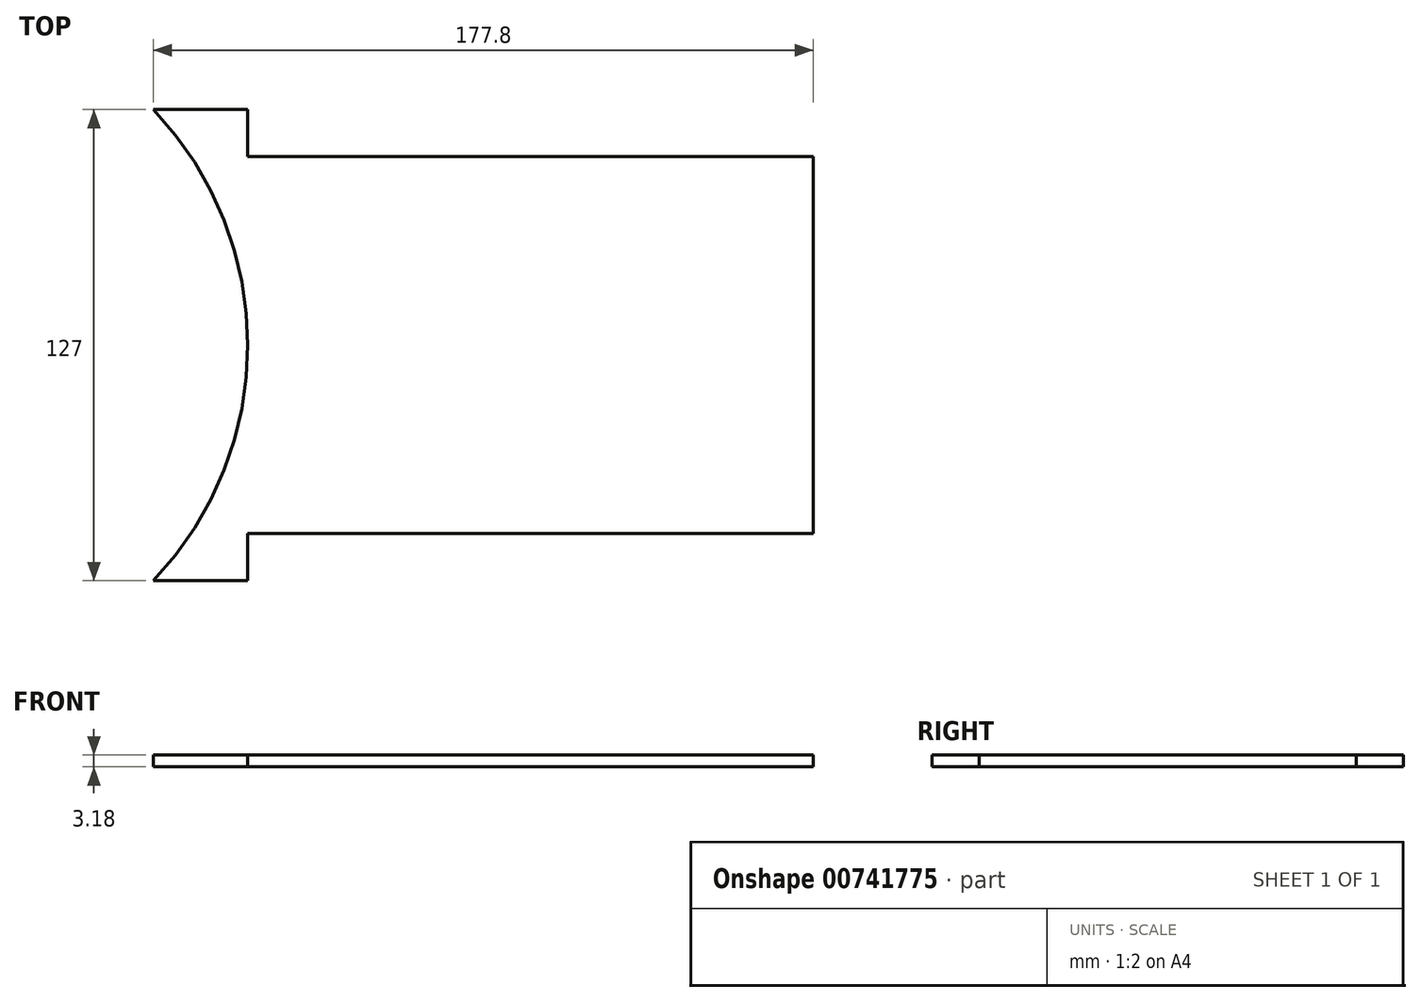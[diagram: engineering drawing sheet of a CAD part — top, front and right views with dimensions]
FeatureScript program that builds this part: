
annotation { "Feature Type Name" : "Feature", "Feature Type Description" : "" }
export const myFeature = defineFeature(function(context is Context, id is Id, definition is map)
    precondition{}
    {
        {
            var Q0;
            Q0=qCreatedBy(makeId("Top.planeOp"),FACE);
            var sketch = newSketch(context, id + "F0", { "sketchPlane" : qUnion([Q0])});
            skLineSegment(sketch, "E0.bottom", {"start": v(-120.07, 14.71) * mm, "end": v(57.73, 14.71) * mm});
            skLineSegment(sketch, "E0.top", {"start": v(-120.07, -86.89) * mm, "end": v(57.73, -86.89) * mm});
            skLineSegment(sketch, "E0.left", {"start": v(-120.07, 14.71) * mm, "end": v(-120.07, -86.89) * mm});
            skLineSegment(sketch, "E0.right", {"start": v(57.73, 14.71) * mm, "end": v(57.73, -86.89) * mm});
            skLineSegment(sketch, "E1.bottom", {"start": v(19.63, 14.71) * mm, "end": v(45.03, 14.71) * mm});
            skLineSegment(sketch, "E1.top", {"start": v(19.63, 11.54) * mm, "end": v(45.03, 11.54) * mm});
            skLineSegment(sketch, "E1.left", {"start": v(19.63, 14.71) * mm, "end": v(19.63, 11.54) * mm});
            skLineSegment(sketch, "E1.right", {"start": v(45.03, 14.71) * mm, "end": v(45.03, 11.54) * mm});
            skLineSegment(sketch, "E2.bottom", {"start": v(19.63, -83.71) * mm, "end": v(45.03, -83.71) * mm});
            skLineSegment(sketch, "E2.top", {"start": v(19.63, -86.89) * mm, "end": v(45.03, -86.89) * mm});
            skLineSegment(sketch, "E2.left", {"start": v(19.63, -83.71) * mm, "end": v(19.63, -86.89) * mm});
            skLineSegment(sketch, "E2.right", {"start": v(45.03, -83.71) * mm, "end": v(45.03, -86.89) * mm});
            skLineSegment(sketch, "E3.bottom", {"start": v(-120.07, 14.71) * mm, "end": v(-120.07, 14.71) * mm});
            skLineSegment(sketch, "E3.top", {"start": v(-120.07, 27.41) * mm, "end": v(-120.07, 27.41) * mm});
            skLineSegment(sketch, "E3.left", {"start": v(-120.07, 14.71) * mm, "end": v(-120.07, 27.41) * mm});
            skLineSegment(sketch, "E3.right", {"start": v(-120.07, 14.71) * mm, "end": v(-120.07, 27.41) * mm});
            skLineSegment(sketch, "E4.top", {"start": v(-89.1, 14.71) * mm, "end": v(-94.67, 14.71) * mm});
            skLineSegment(sketch, "E4.right", {"start": v(-94.67, 27.41) * mm, "end": v(-94.67, 14.71) * mm});
            skLineSegment(sketch, "E5.bottom", {"start": v(-120.07, 27.41) * mm, "end": v(-94.67, 27.41) * mm});
            skPoint(sketch, "E4.left.start.orphan", {"position": v(-89.1, 27.41) * mm});
            skLineSegment(sketch, "E6.bottom", {"start": v(-120.07, -86.89) * mm, "end": v(-120.07, -86.89) * mm});
            skLineSegment(sketch, "E6.top", {"start": v(-120.07, -99.59) * mm, "end": v(-120.07, -99.59) * mm});
            skLineSegment(sketch, "E6.left", {"start": v(-120.07, -86.89) * mm, "end": v(-120.07, -99.59) * mm});
            skLineSegment(sketch, "E6.right", {"start": v(-120.07, -86.89) * mm, "end": v(-120.07, -99.59) * mm});
            skLineSegment(sketch, "E7.bottom", {"start": v(-94.67, -99.59) * mm, "end": v(-94.67, -99.59) * mm});
            skLineSegment(sketch, "E7.top", {"start": v(-94.67, -86.89) * mm, "end": v(-94.67, -86.89) * mm});
            skLineSegment(sketch, "E7.left", {"start": v(-94.67, -99.59) * mm, "end": v(-94.67, -86.89) * mm});
            skLineSegment(sketch, "E7.right", {"start": v(-94.67, -99.59) * mm, "end": v(-94.67, -86.89) * mm});
            skLineSegment(sketch, "E8.bottom", {"start": v(-94.67, -99.59) * mm, "end": v(-120.07, -99.59) * mm});
            skLineSegment(sketch, "E8.top", {"start": v(-94.67, -99.59) * mm, "end": v(-120.07, -99.59) * mm});
            skArc(sketch, "E9", {"start": v(-120.07, -99.59) * mm, "mid": v(-94.67, -36.09) * mm, "end": v(-120.07, 27.41) * mm});
            skSolve(sketch);
        }
        {
            var Q0;
            {var subQ0=sQuery(id+"F0.wireOp",EDGE,"E4.right");var subQ7=sQuery(id+"F0.wireOp",EDGE,"E3.left");var subQ11=sQuery(id+"F0.wireOp",EDGE,"E6.left");var subQ12=sQuery(id+"F0.wireOp",EDGE,"E0.left");var subQ21=makeQuery(id+"F0.imprint","IMPRINT",EDGE,{"derivedFrom":sQuery(id+"F0.wireOp",EDGE,"E2.bottom")});var subQ23=sQuery(id+"F0.wireOp",EDGE,"E0.right");var subQ24=sQuery(id+"F0.wireOp",EDGE,"E7.left");var subQ30=makeQuery(id+"F0.imprint","IMPRINT",EDGE,{"derivedFrom":sQuery(id+"F0.wireOp",EDGE,"E1.top")});Q0=qUnion([makeQuery(id+"F0.imprint","IMPRINT",FACE,{"disambiguationData":[TD([[makeQuery(id+"F0.imprint","IMPRINT",EDGE,{"derivedFrom":subQ7}),-1.0]])]}),makeQuery(id+"F0.imprint","IMPRINT",FACE,{"disambiguationData":[TD([[makeQuery(id+"F0.imprint","IMPRINT",EDGE,{"derivedFrom":subQ12}),1.0]])]}),makeQuery(id+"F0.imprint","IMPRINT",FACE,{"disambiguationData":[TD([[subQ30,1.0]])]}),makeQuery(id+"F0.imprint","IMPRINT",FACE,{"disambiguationData":[TD([[makeQuery(id+"F0.imprint","IMPRINT",EDGE,{"derivedFrom":subQ24}),1.0]])]}),makeQuery(id+"F0.imprint","IMPRINT",FACE,{"disambiguationData":[TD([[makeQuery(id+"F0.imprint","IMPRINT",EDGE,{"derivedFrom":subQ23}),-1.0]])]}),makeQuery(id+"F0.imprint","IMPRINT",FACE,{"disambiguationData":[TD([[subQ21,-1.0]])]}),makeQuery(id+"F0.imprint","IMPRINT",FACE,{"disambiguationData":[TD([[makeQuery(id+"F0.imprint","IMPRINT",EDGE,{"derivedFrom":subQ11}),1.0]])]}),makeQuery(id+"F0.imprint","IMPRINT",FACE,{"disambiguationData":[TD([[makeQuery(id+"F0.imprint","IMPRINT",EDGE,{"derivedFrom":subQ0}),-1.0]])]})]);}
            extrude(context, id + "F1", {"entities" : qUnion([Q0]), "depth" : 3.17 * mm, "offsetDistance" : 25.4 * mm});
        }
        {
            var Q0;
            Q0=sQuery(id+"F0.wireOp",EDGE,"E1.top");
            var Q1;
            Q1=sQuery(id+"F0.wireOp",EDGE,"E1.left");
            var Q2;
            Q2=sQuery(id+"F0.wireOp",EDGE,"E1.right");
            extrude(context, id + "F2", {"bodyType" : ToolBodyType.SURFACE, "surfaceEntities" : qUnion([Q0, Q1, Q2]), "depth" : 25.4 * mm, "offsetDistance" : 25.4 * mm});
        }
        {
            var Q0;
            Q0=sQuery(id+"F0.wireOp",EDGE,"E2.bottom");
            var Q1;
            Q1=sQuery(id+"F0.wireOp",EDGE,"E2.top");
            var Q2;
            Q2=sQuery(id+"F0.wireOp",EDGE,"E2.right");
            var Q3;
            Q3=sQuery(id+"F0.wireOp",EDGE,"E2.left");
            extrude(context, id + "F3", {"bodyType" : ToolBodyType.SURFACE, "surfaceEntities" : qUnion([Q0, Q1, Q2, Q3]), "depth" : 25.4 * mm, "offsetDistance" : 25.4 * mm});
        }
        {
            var Q0;
            Q0=makeQuery(id+"F3.opExtrude","SWEPT_FACE",FACE,{"disambiguationData":[OSD([sQuery(id+"F0.wireOp",EDGE,"E2.top")])]});
            var sketch = newSketch(context, id + "F4", { "sketchPlane" : qUnion([Q0])});
            skCircle(sketch, "E10", {"center": v(-32.33, 12.7) * mm, "radius": 2.54 * mm});
            skPoint(sketch, "E10.centerSnap0", {"position": v(-19.63, 12.7) * mm});
            skPoint(sketch, "E10.centerSnap1", {"position": v(-32.33, 25.4) * mm});
            skSolve(sketch);
        }
        {
            var Q0;
            Q0=makeQuery(id+"F4.imprint","IMPRINT",FACE,{"disambiguationData":[TD([[makeQuery(id+"F4.imprint","IMPRINT",EDGE,{"derivedFrom":sQuery(id+"F4.wireOp",EDGE,"E10")}),1.0]])]});
            var Q1;
            Q1=sQuery(id+"F4.wireOp",EDGE,"E10");
            extrude(context, id + "F5", {"entities" : qUnion([Q0]), "bodyType" : ToolBodyType.SURFACE, "operationType" : NewBodyOperationType.REMOVE, "surfaceEntities" : qUnion([Q1]), "depth" : 127 * mm, "offsetDistance" : 25.4 * mm, "hasSecondDirection" : true, "secondDirectionOppositeDirection" : true, "secondDirectionDepth" : 25.4 * mm});
        }
        {
            var Q0;
            {var subQ0=sQuery(id+"F0.wireOp",EDGE,"E0.left");Q0=makeQuery(id+"F0.imprint","IMPRINT",FACE,{"disambiguationData":[TD([[makeQuery(id+"F0.imprint","IMPRINT",EDGE,{"derivedFrom":subQ0}),1.0]])]});}
            var Q1;
            {var subQ0=sQuery(id+"F0.wireOp",EDGE,"E3.left");Q1=makeQuery(id+"F0.imprint","IMPRINT",FACE,{"disambiguationData":[TD([[makeQuery(id+"F0.imprint","IMPRINT",EDGE,{"derivedFrom":subQ0}),-1.0]])]});}
            var Q2;
            {var subQ3=sQuery(id+"F0.wireOp",EDGE,"E6.left");Q2=makeQuery(id+"F0.imprint","IMPRINT",FACE,{"disambiguationData":[TD([[makeQuery(id+"F0.imprint","IMPRINT",EDGE,{"derivedFrom":subQ3}),1.0]])]});}
            extrude(context, id + "F6", {"entities" : qUnion([Q0, Q1, Q2]), "operationType" : NewBodyOperationType.REMOVE, "endBound" : BoundingType.THROUGH_ALL, "depth" : 25.4 * mm, "offsetDistance" : 25.4 * mm});
        }
    });
